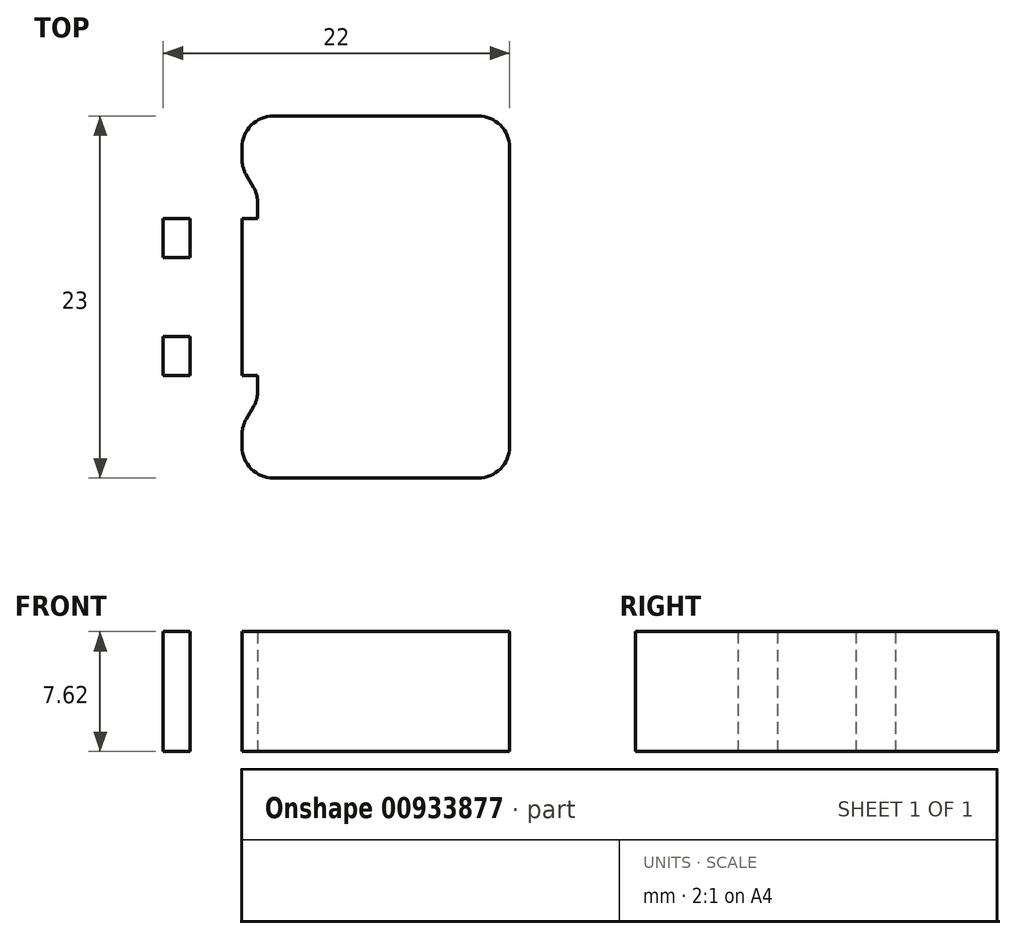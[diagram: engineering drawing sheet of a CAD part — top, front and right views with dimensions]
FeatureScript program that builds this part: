
annotation { "Feature Type Name" : "Feature", "Feature Type Description" : "" }
export const myFeature = defineFeature(function(context is Context, id is Id, definition is map)
    precondition{}
    {
        {
            var Q0;
            Q0=qCreatedBy(makeId("Top.planeOp"),FACE);
            var sketch = newSketch(context, id + "F0", { "sketchPlane" : qUnion([Q0])});
            skLineSegment(sketch, "E0.bottom", {"start": v(6.5, -11.5) * mm, "end": v(-6.5, -11.5) * mm});
            skLineSegment(sketch, "E0.top", {"start": v(6.5, 11.5) * mm, "end": v(-6.5, 11.5) * mm});
            skLineSegment(sketch, "E0.left", {"start": v(8.5, -9.5) * mm, "end": v(8.5, 9.5) * mm});
            skLineSegment(sketch, "E0.right", {"start": v(-8.5, -9.5) * mm, "end": v(-8.5, -8.77) * mm});
            skPoint(sketch, "E0.middle", {"position": v(0, 0) * mm});
            skLineSegment(sketch, "E1.bottom", {"start": v(-11.8, -2.5) * mm, "end": v(-13.5, -2.5) * mm});
            skLineSegment(sketch, "E1.top", {"start": v(-11.8, -5) * mm, "end": v(-13.5, -5) * mm});
            skLineSegment(sketch, "E1.left", {"start": v(-11.8, -2.5) * mm, "end": v(-11.8, -5) * mm});
            skLineSegment(sketch, "E1.right", {"start": v(-13.5, -2.5) * mm, "end": v(-13.5, -5) * mm});
            skPoint(sketch, "E1.middle", {"position": v(-12.65, -3.75) * mm});
            skLineSegment(sketch, "E2.bottom", {"start": v(-13.5, 5) * mm, "end": v(-11.8, 5) * mm});
            skLineSegment(sketch, "E2.top", {"start": v(-13.5, 2.5) * mm, "end": v(-11.8, 2.5) * mm});
            skLineSegment(sketch, "E2.left", {"start": v(-13.5, 5) * mm, "end": v(-13.5, 2.5) * mm});
            skLineSegment(sketch, "E2.right", {"start": v(-11.8, 5) * mm, "end": v(-11.8, 2.5) * mm});
            skPoint(sketch, "E2.middle", {"position": v(-12.65, 3.75) * mm});
            skLineSegment(sketch, "E3", {"start": v(-12.65, 3.75) * mm, "end": v(-12.65, -3.75) * mm, "construction": true});
            skLineSegment(sketch, "E4", {"start": v(0, 0) * mm, "end": v(-12.65, 0) * mm, "construction": true});
            skLineSegment(sketch, "E5.bottom", {"start": v(-0.25, -11) * mm, "end": v(-7.25, -11) * mm, "construction": true});
            skLineSegment(sketch, "E5.top", {"start": v(-0.25, 11) * mm, "end": v(-7.25, 11) * mm, "construction": true});
            skLineSegment(sketch, "E5.left", {"start": v(-0.25, -11) * mm, "end": v(-0.25, 11) * mm, "construction": true});
            skLineSegment(sketch, "E5.right", {"start": v(-7.25, -11) * mm, "end": v(-7.25, 11) * mm, "construction": true});
            skPoint(sketch, "E5.middle", {"position": v(-3.75, 0) * mm});
            skPoint(sketch, "E6.visualSharp", {"position": v(-8.5, -11.5) * mm});
            skArc(sketch, "E6.filletArc", {"start": v(-8.5, -9.5) * mm, "mid": v(-7.91, -10.91) * mm, "end": v(-6.5, -11.5) * mm});
            skPoint(sketch, "E7.visualSharp", {"position": v(-8.5, 11.5) * mm});
            skArc(sketch, "E7.filletArc", {"start": v(-6.5, 11.5) * mm, "mid": v(-7.91, 10.91) * mm, "end": v(-8.5, 9.5) * mm});
            skPoint(sketch, "E8.visualSharp", {"position": v(8.5, 11.5) * mm});
            skArc(sketch, "E8.filletArc", {"start": v(8.5, 9.5) * mm, "mid": v(7.91, 10.91) * mm, "end": v(6.5, 11.5) * mm});
            skPoint(sketch, "E9.visualSharp", {"position": v(8.5, -11.5) * mm});
            skArc(sketch, "E9.filletArc", {"start": v(6.5, -11.5) * mm, "mid": v(7.91, -10.91) * mm, "end": v(8.5, -9.5) * mm});
            skLineSegment(sketch, "E10.bottom", {"start": v(-8.5, -5) * mm, "end": v(-7.5, -5) * mm});
            skLineSegment(sketch, "E10.right", {"start": v(-7.5, -5) * mm, "end": v(-7.5, -5.96) * mm});
            skPoint(sketch, "E10.middle", {"position": v(-8, -5.75) * mm});
            skLineSegment(sketch, "E11", {"start": v(-7.77, -6.96) * mm, "end": v(-8.23, -7.77) * mm});
            skPoint(sketch, "E12.visualSharp", {"position": v(-7.5, -6.5) * mm});
            skArc(sketch, "E12.filletArc", {"start": v(-7.77, -6.96) * mm, "mid": v(-7.57, -6.48) * mm, "end": v(-7.5, -5.96) * mm});
            skArc(sketch, "E13.filletArc", {"start": v(-8.23, -7.77) * mm, "mid": v(-8.43, -8.25) * mm, "end": v(-8.5, -8.77) * mm});
            skLineSegment(sketch, "E14", {"start": v(-8.5, -5) * mm, "end": v(-8.5, 0) * mm});
            skArc(sketch, "E15.MirrorCS", {"start": v(-8.23, 7.77) * mm, "mid": v(-8.43, 8.25) * mm, "end": v(-8.5, 8.77) * mm});
            skLineSegment(sketch, "E16.MirrorCS", {"start": v(-8.5, 9.5) * mm, "end": v(-8.5, 8.77) * mm});
            skLineSegment(sketch, "E17.MirrorCS", {"start": v(-7.77, 6.96) * mm, "end": v(-8.23, 7.77) * mm});
            skPoint(sketch, "E18.MirrorP", {"position": v(-7.5, 6.5) * mm});
            skArc(sketch, "E19.MirrorCS", {"start": v(-7.77, 6.96) * mm, "mid": v(-7.57, 6.48) * mm, "end": v(-7.5, 5.96) * mm});
            skLineSegment(sketch, "E20.MirrorCS", {"start": v(-7.5, 5) * mm, "end": v(-7.5, 5.96) * mm});
            skLineSegment(sketch, "E21.MirrorCS", {"start": v(-8.5, 5) * mm, "end": v(-7.5, 5) * mm});
            skLineSegment(sketch, "E22.MirrorCS", {"start": v(-8.5, 5) * mm, "end": v(-8.5, 0) * mm});
            skSolve(sketch);
        }
        {
            var Q0;
            Q0=makeQuery(id+"F0.imprint","IMPRINT",FACE,{"disambiguationData":[TD([[makeQuery(id+"F0.imprint","IMPRINT",EDGE,{"derivedFrom":sQuery(id+"F0.wireOp",EDGE,"E0.bottom")}),1.0]])]});
            var Q1;
            Q1=makeQuery(id+"F0.imprint","IMPRINT",FACE,{"disambiguationData":[TD([[makeQuery(id+"F0.imprint","IMPRINT",EDGE,{"derivedFrom":sQuery(id+"F0.wireOp",EDGE,"E0.bottom")}),-1.0]])]});
            var Q2;
            Q2=makeQuery(id+"F0.imprint","IMPRINT",FACE,{"disambiguationData":[TD([[makeQuery(id+"F0.imprint","IMPRINT",EDGE,{"derivedFrom":sQuery(id+"F0.wireOp",EDGE,"E1.bottom")}),1.0]])]});
            var Q3;
            Q3=makeQuery(id+"F0.imprint","IMPRINT",FACE,{"disambiguationData":[TD([[makeQuery(id+"F0.imprint","IMPRINT",EDGE,{"derivedFrom":sQuery(id+"F0.wireOp",EDGE,"E2.bottom")}),-1.0]])]});
            extrude(context, id + "F1", {"entities" : qUnion([Q0, Q1, Q2, Q3]), "depth" : 7.62 * mm, "offsetDistance" : 25 * mm});
        }
    });
